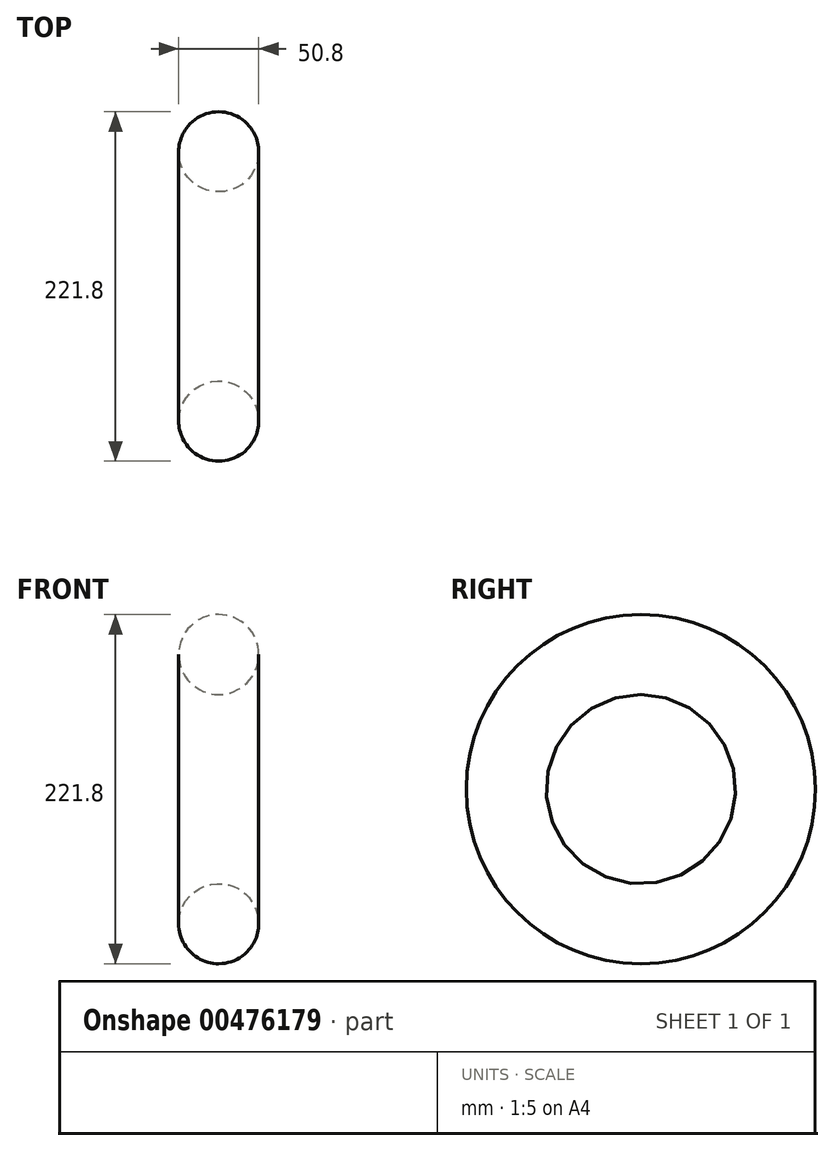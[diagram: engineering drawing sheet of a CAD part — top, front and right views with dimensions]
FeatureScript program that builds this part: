
annotation { "Feature Type Name" : "Feature", "Feature Type Description" : "" }
export const myFeature = defineFeature(function(context is Context, id is Id, definition is map)
    precondition{}
    {
        {
            var Q0;
            Q0=qCreatedBy(makeId("Top.planeOp"),FACE);
            var sketch = newSketch(context, id + "F0", { "sketchPlane" : qUnion([Q0])});
            skCircle(sketch, "E0", {"center": v(0, 0) * mm, "radius": 25.4 * mm});
            skLineSegment(sketch, "E1", {"start": v(-55.35, -85.5) * mm, "end": v(97.05, -85.5) * mm});
            skSolve(sketch);
        }
        {
            var Q0;
            Q0=makeQuery(id+"F0.imprint","IMPRINT",FACE,{"disambiguationData":[TD([[makeQuery(id+"F0.imprint","IMPRINT",EDGE,{"derivedFrom":sQuery(id+"F0.wireOp",EDGE,"E0")}),1.0]])]});
            var Q1;
            Q1=sQuery(id+"F0.wireOp",EDGE,"E1");
            revolve(context, id + "F1", {"entities" : qUnion([Q0]), "axis" : qUnion([Q1]), "revolveType" : RevolveType.FULL});
        }
    });
